# Revit family: SURE-BOARD-SERIES200S-F
name_source: partatom
category: Generic Models
units: mm (PartAtom-declared; Revit-internal decimal feet)

## family parameters
Can host rebar = No
Cut with Voids When Loaded = No
Host = Face
Maintain Annotation Orientation = No
Part Type = Normal
Room Calculation Point = No
Round Connector Dimension = Use Diameter
Shared = No

## types (1)
- 200S-F
    Assembly Code = B1010220
    Default Elevation = 4' - 0"
    Description = SureBoard Series 200S-F for Floors and Flat Roof Decks
    FCSheathingThickness = 0' - 0 9/16"
    Height = 4' - 0"
    Keynote = 054000
    Manufacturer = California  Expanded Metal Lath Products Co. (CEMCO)
    Overlap = 0' - 2"
    Product Info = Sure-Board® Series 200S-F Sheathing for Floors and Flat Roofs
    Product Submittal Link = https://cemcosteel.com
    SteelSheetThickness = 0' - 0 1/32"
    URL = http://www.cemcosteel.com
    Width = 4' - 0"

## geometry (parser evidence)
native form markers: Sweep x2
no freeform markers — native parametric forms only
